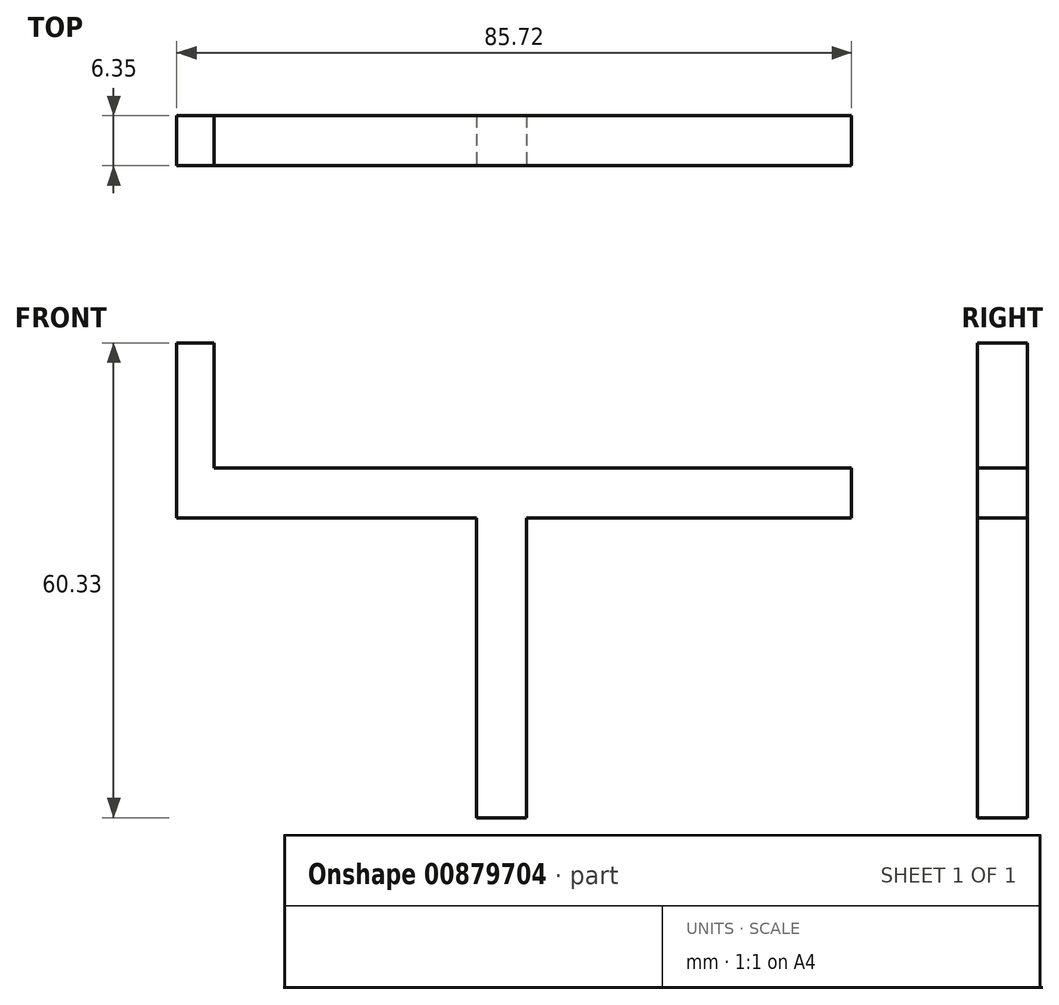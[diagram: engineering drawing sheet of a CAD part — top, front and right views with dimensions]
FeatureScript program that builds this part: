
annotation { "Feature Type Name" : "Feature", "Feature Type Description" : "" }
export const myFeature = defineFeature(function(context is Context, id is Id, definition is map)
    precondition{}
    {
        {
            var Q0;
            Q0=qCreatedBy(makeId("Front.planeOp"),FACE);
            var sketch = newSketch(context, id + "F0", { "sketchPlane" : qUnion([Q0])});
            skLineSegment(sketch, "E0.bottom", {"start": v(-45.84, 40.2) * mm, "end": v(39.88, 40.2) * mm});
            skLineSegment(sketch, "E0.top", {"start": v(-45.84, 33.85) * mm, "end": v(39.88, 33.85) * mm});
            skLineSegment(sketch, "E0.left", {"start": v(-45.84, 40.2) * mm, "end": v(-45.84, 33.85) * mm});
            skLineSegment(sketch, "E0.right", {"start": v(39.88, 40.2) * mm, "end": v(39.88, 33.85) * mm});
            skSolve(sketch);
        }
        {
            var Q0;
            Q0 = qSketchRegion(id + "F0", true);
            extrude(context, id + "F1", {"entities" : qUnion([Q0]), "depth" : 6.35 * mm, "offsetDistance" : 25.4 * mm});
        }
        {
            var Q0;
            Q0=makeQuery(id+"F1.opExtrude","SWEPT_FACE",FACE,{"disambiguationData":[OSD([sQuery(id+"F0.wireOp",EDGE,"E0.left")])]});
            var sketch = newSketch(context, id + "F2", { "sketchPlane" : qUnion([Q0])});
            skPoint(sketch, "E1.oppositeSnap0", {"position": v(6.35, 37.03) * mm});
            skLineSegment(sketch, "E1.bottom", {"start": v(0, 33.85) * mm, "end": v(6.35, 33.85) * mm});
            skLineSegment(sketch, "E1.top", {"start": v(0, 56.08) * mm, "end": v(6.35, 56.08) * mm});
            skLineSegment(sketch, "E1.left", {"start": v(0, 33.85) * mm, "end": v(0, 56.08) * mm});
            skLineSegment(sketch, "E1.right", {"start": v(6.35, 33.85) * mm, "end": v(6.35, 56.08) * mm});
            skSolve(sketch);
        }
        {
            var Q0;
            Q0 = qSketchRegion(id + "F2", true);
            extrude(context, id + "F3", {"entities" : qUnion([Q0]), "operationType" : NewBodyOperationType.ADD, "oppositeDirection" : true, "depth" : 4.76 * mm, "offsetDistance" : 25.4 * mm});
        }
        {
            var Q0;
            Q0=makeQuery(id+"F1.opExtrude","SWEPT_FACE",FACE,{"disambiguationData":[OSD([sQuery(id+"F0.wireOp",EDGE,"E0.top")])]});
            var sketch = newSketch(context, id + "F4", { "sketchPlane" : qUnion([Q0])});
            skLineSegment(sketch, "E2.bottom", {"start": v(-7.74, 0) * mm, "end": v(-1.4, 0) * mm});
            skLineSegment(sketch, "E2.top", {"start": v(-7.74, 6.35) * mm, "end": v(-1.4, 6.35) * mm});
            skLineSegment(sketch, "E2.left", {"start": v(-7.74, 0) * mm, "end": v(-7.74, 6.35) * mm});
            skLineSegment(sketch, "E2.right", {"start": v(-1.4, 0) * mm, "end": v(-1.4, 6.35) * mm});
            skSolve(sketch);
        }
        {
            var Q0;
            Q0 = qSketchRegion(id + "F4", true);
            extrude(context, id + "F5", {"entities" : qUnion([Q0]), "operationType" : NewBodyOperationType.ADD, "depth" : 38.1 * mm, "offsetDistance" : 25.4 * mm});
        }
    });
